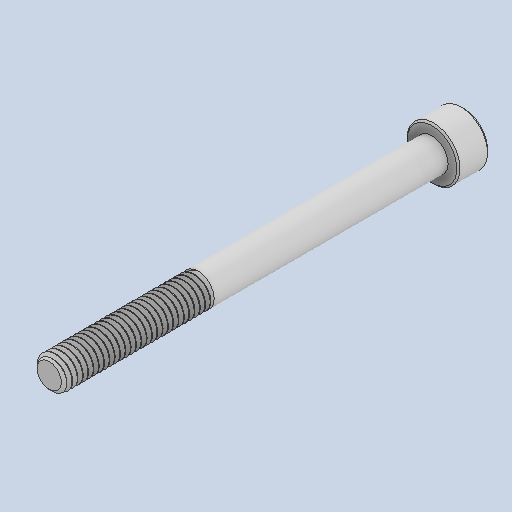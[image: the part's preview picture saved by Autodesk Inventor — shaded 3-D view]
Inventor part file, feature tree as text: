
AUTODESK INVENTOR PART (.ipt)
format: ipt  version: 2022.3 (Build 263350000, 350)  size: 693,248 bytes
history: native  units: in
note: dims shown in document units (in); Inventor stores cm internally (conversion verified against a paired STEP export)
features: chamfer x1
ambient origin geometry x8: Origin, YZ Plane, XZ Plane, XY Plane, X Axis, Y Axis, Z Axis, Center Point
bodies: Solid1 (feature_tree)
feature tree (1):
  chamfer  "Chamfer2"  [1 undecoded]
note: 1 required parameter value undecoded (feature->parameter linkage not recoverable at this tier; creation-order binding heuristic only, values carry confidence <= 0.55)
